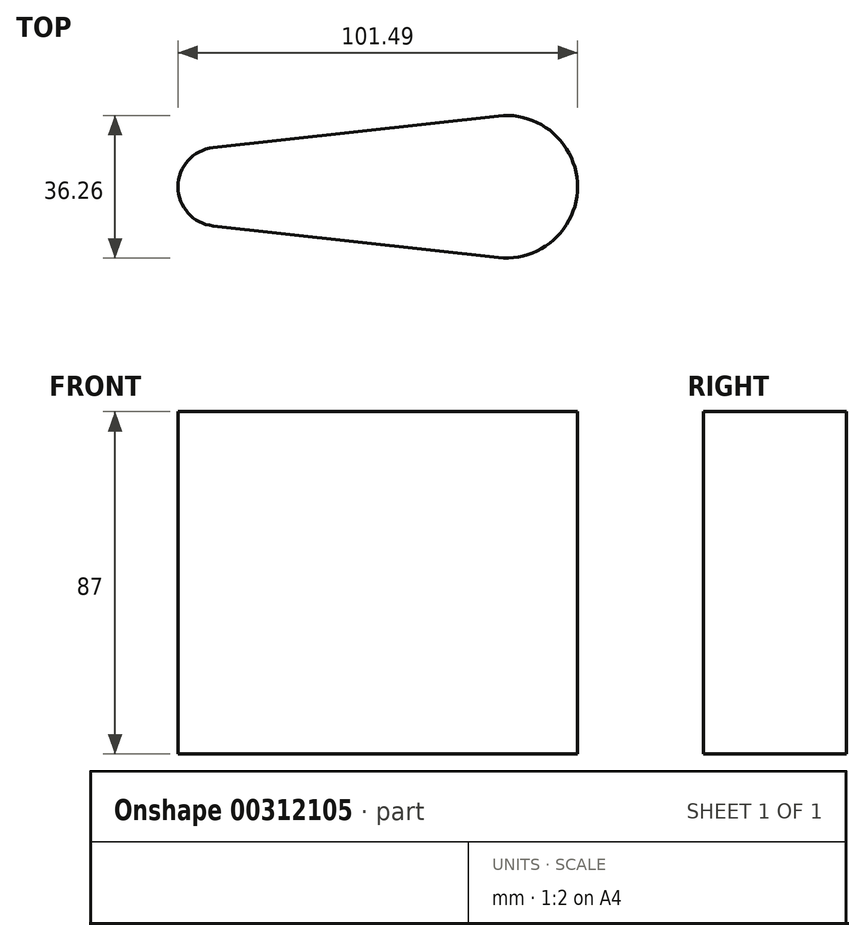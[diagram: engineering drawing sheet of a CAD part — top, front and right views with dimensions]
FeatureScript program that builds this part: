
annotation { "Feature Type Name" : "Feature", "Feature Type Description" : "" }
export const myFeature = defineFeature(function(context is Context, id is Id, definition is map)
    precondition{}
    {
        {
            var Q0;
            Q0=qCreatedBy(makeId("Top.planeOp"),FACE);
            var sketch = newSketch(context, id + "F0", { "sketchPlane" : qUnion([Q0])});
            skCircle(sketch, "E0", {"center": v(-41.87, 21.22) * mm, "radius": 10 * mm});
            skCircle(sketch, "E1", {"center": v(31.49, 21.22) * mm, "radius": 18.13 * mm});
            skLineSegment(sketch, "E2", {"start": v(-42.98, 31.16) * mm, "end": v(29.48, 39.24) * mm});
            skLineSegment(sketch, "E3", {"start": v(-42.98, 11.28) * mm, "end": v(29.48, 3.2) * mm});
            skLineSegment(sketch, "E4", {"start": v(-41.87, 21.22) * mm, "end": v(60.34, 21.22) * mm, "construction": true});
            skSolve(sketch);
        }
        {
            assignVariable(context, id + "F1", {"name" : "myvar", "anyValue" : 87});
        }
        {
            var Q0;
            Q0 = qSketchRegion(id + "F0", true);
            extrude(context, id + "F2", {"entities" : qUnion([Q0]), "depth" : (getVariable(context, 'myvar')) * mm});
        }
    });
